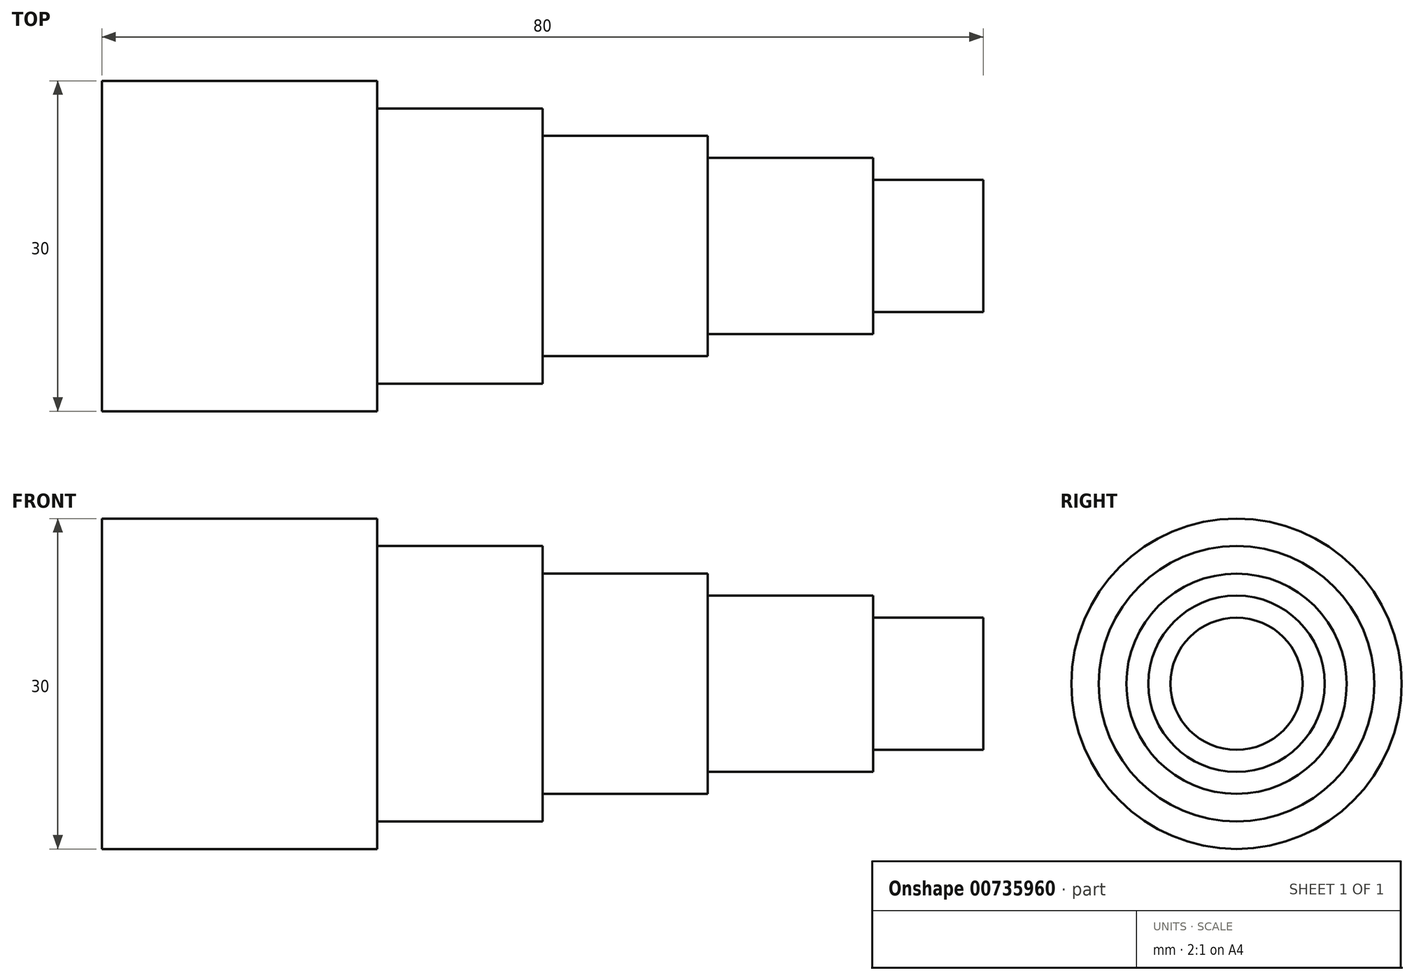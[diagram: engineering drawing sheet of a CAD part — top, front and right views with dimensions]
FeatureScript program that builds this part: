
annotation { "Feature Type Name" : "Feature", "Feature Type Description" : "" }
export const myFeature = defineFeature(function(context is Context, id is Id, definition is map)
    precondition{}
    {
        {
            var Q0;
            Q0=qCreatedBy(makeId("Top.planeOp"),FACE);
            var sketch = newSketch(context, id + "F0", { "sketchPlane" : qUnion([Q0])});
            skLineSegment(sketch, "E0", {"start": v(80, 0) * mm, "end": v(0, 0) * mm});
            skLineSegment(sketch, "E1.bottom", {"start": v(0, 0) * mm, "end": v(25, 0) * mm});
            skLineSegment(sketch, "E1.top", {"start": v(0, 15) * mm, "end": v(25, 15) * mm});
            skLineSegment(sketch, "E1.left", {"start": v(0, 0) * mm, "end": v(0, 15) * mm});
            skLineSegment(sketch, "E1.right", {"start": v(25, 0) * mm, "end": v(25, 15) * mm});
            skPoint(sketch, "E2.oppositeSnap0", {"position": v(40, 0) * mm});
            skLineSegment(sketch, "E2.bottom", {"start": v(25, 12.5) * mm, "end": v(40, 12.5) * mm});
            skLineSegment(sketch, "E2.top", {"start": v(25, 0) * mm, "end": v(40, 0) * mm});
            skLineSegment(sketch, "E2.left", {"start": v(25, 12.5) * mm, "end": v(25, 0) * mm});
            skLineSegment(sketch, "E2.right", {"start": v(40, 12.5) * mm, "end": v(40, 0) * mm});
            skLineSegment(sketch, "E3.bottom", {"start": v(40, 0) * mm, "end": v(55, 0) * mm});
            skLineSegment(sketch, "E3.top", {"start": v(40, 10) * mm, "end": v(55, 10) * mm});
            skLineSegment(sketch, "E3.left", {"start": v(40, 0) * mm, "end": v(40, 10) * mm});
            skLineSegment(sketch, "E3.right", {"start": v(55, 0) * mm, "end": v(55, 10) * mm});
            skLineSegment(sketch, "E4.bottom", {"start": v(55, 8) * mm, "end": v(70, 8) * mm});
            skLineSegment(sketch, "E4.top", {"start": v(55, 0) * mm, "end": v(70, 0) * mm});
            skLineSegment(sketch, "E4.left", {"start": v(55, 8) * mm, "end": v(55, 0) * mm});
            skLineSegment(sketch, "E4.right", {"start": v(70, 8) * mm, "end": v(70, 0) * mm});
            skLineSegment(sketch, "E5.bottom", {"start": v(70, 0) * mm, "end": v(80, 0) * mm});
            skLineSegment(sketch, "E5.top", {"start": v(70, 6) * mm, "end": v(80, 6) * mm});
            skLineSegment(sketch, "E5.left", {"start": v(70, 0) * mm, "end": v(70, 6) * mm});
            skLineSegment(sketch, "E5.right", {"start": v(80, 0) * mm, "end": v(80, 6) * mm});
            skSolve(sketch);
        }
        {
            var Q0;
            {var subQ5=sQuery(id+"F0.wireOp",EDGE,"E1.top");Q0=makeQuery(id+"F0.imprint","IMPRINT",FACE,{"disambiguationData":[TD([[makeQuery(id+"F0.imprint","IMPRINT",EDGE,{"derivedFrom":subQ5}),-1.0]])]});}
            var Q1;
            {var subQ4=sQuery(id+"F0.wireOp",EDGE,"E2.bottom");Q1=makeQuery(id+"F0.imprint","IMPRINT",FACE,{"disambiguationData":[TD([[makeQuery(id+"F0.imprint","IMPRINT",EDGE,{"derivedFrom":subQ4}),-1.0]])]});}
            var Q2;
            {var subQ0=sQuery(id+"F0.wireOp",EDGE,"E3.top");Q2=makeQuery(id+"F0.imprint","IMPRINT",FACE,{"disambiguationData":[TD([[makeQuery(id+"F0.imprint","IMPRINT",EDGE,{"derivedFrom":subQ0}),-1.0]])]});}
            var Q3;
            {var subQ0=sQuery(id+"F0.wireOp",EDGE,"E4.bottom");Q3=makeQuery(id+"F0.imprint","IMPRINT",FACE,{"disambiguationData":[TD([[makeQuery(id+"F0.imprint","IMPRINT",EDGE,{"derivedFrom":subQ0}),-1.0]])]});}
            var Q4;
            {var subQ4=sQuery(id+"F0.wireOp",EDGE,"E5.top");Q4=makeQuery(id+"F0.imprint","IMPRINT",FACE,{"disambiguationData":[TD([[makeQuery(id+"F0.imprint","IMPRINT",EDGE,{"derivedFrom":subQ4}),-1.0]])]});}
            var Q5;
            Q5=sQuery(id+"F0.wireOp",EDGE,"E2.top");
            revolve(context, id + "F1", {"surfaceOperationType" : NewSurfaceOperationType.NEW, "entities" : qUnion([Q0, Q1, Q2, Q3, Q4]), "axis" : qUnion([Q5]), "revolveType" : RevolveType.FULL});
        }
    });
